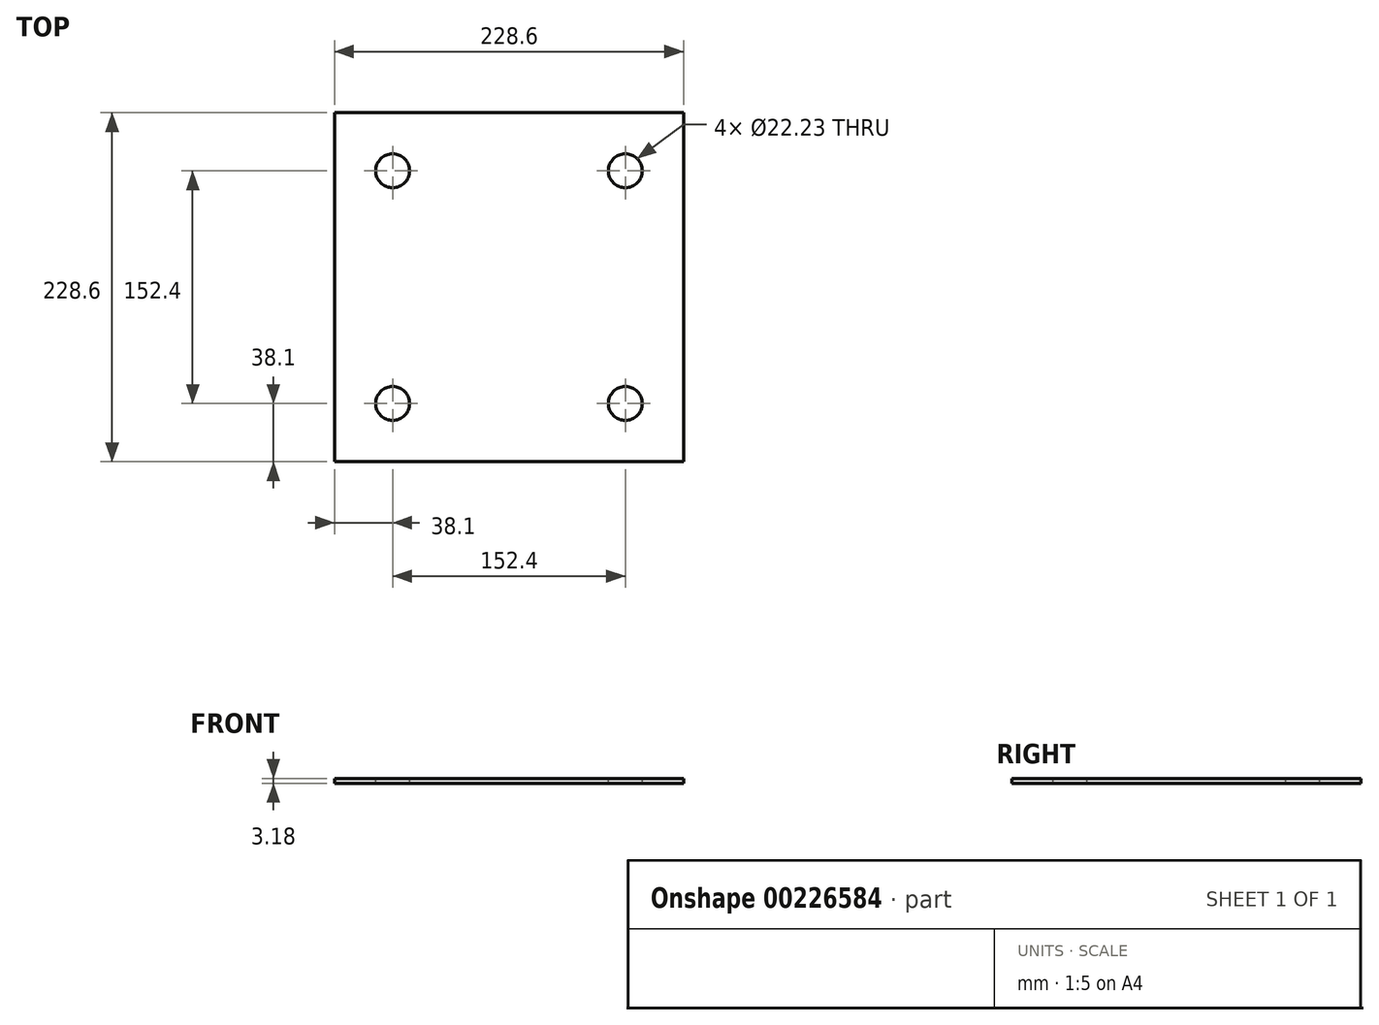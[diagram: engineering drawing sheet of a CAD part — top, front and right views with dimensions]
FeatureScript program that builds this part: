
annotation { "Feature Type Name" : "Feature", "Feature Type Description" : "" }
export const myFeature = defineFeature(function(context is Context, id is Id, definition is map)
    precondition{}
    {
        {
            var Q0;
            Q0=qCreatedBy(makeId("Top.planeOp"),FACE);
            var sketch = newSketch(context, id + "F0", { "sketchPlane" : qUnion([Q0])});
            skLineSegment(sketch, "E0.bottom", {"start": v(114.3, 114.3) * mm, "end": v(-114.3, 114.3) * mm});
            skLineSegment(sketch, "E0.top", {"start": v(114.3, -114.3) * mm, "end": v(-114.3, -114.3) * mm});
            skLineSegment(sketch, "E0.left", {"start": v(114.3, 114.3) * mm, "end": v(114.3, -114.3) * mm});
            skLineSegment(sketch, "E0.right", {"start": v(-114.3, 114.3) * mm, "end": v(-114.3, -114.3) * mm});
            skPoint(sketch, "E0.middle", {"position": v(0, 0) * mm});
            skSolve(sketch);
        }
        {
            var Q0;
            Q0=qSketchRegion(id+"F0",true);
            extrude(context, id + "F1", {"entities" : qUnion([Q0]), "oppositeDirection" : true, "depth" : 3.17 * mm, "symmetric" : true});
        }
        {
            var Q0;
            Q0=makeQuery(id+"F1.opExtrude","CAP_FACE",FACE,{"disambiguationData":[OSD([sQuery(id+"F0.wireOp",EDGE,"E0.bottom"),sQuery(id+"F0.wireOp",EDGE,"E0.top"),sQuery(id+"F0.wireOp",EDGE,"E0.left"),sQuery(id+"F0.wireOp",EDGE,"E0.right")])],"isStart":true});
            var sketch = newSketch(context, id + "F2", { "sketchPlane" : qUnion([Q0])});
            skLineSegment(sketch, "E1.bottom", {"start": v(76.2, 76.2) * mm, "end": v(-76.2, 76.2) * mm});
            skLineSegment(sketch, "E1.top", {"start": v(76.2, -76.2) * mm, "end": v(-76.2, -76.2) * mm});
            skLineSegment(sketch, "E1.left", {"start": v(76.2, 76.2) * mm, "end": v(76.2, -76.2) * mm});
            skLineSegment(sketch, "E1.right", {"start": v(-76.2, 76.2) * mm, "end": v(-76.2, -76.2) * mm});
            skPoint(sketch, "E1.middle", {"position": v(0, 0) * mm});
            skSolve(sketch);
        }
        {
            var Q0;
            Q0=sQuery(id+"F2.wireOp",VERTEX,"E1.right.start");
            var Q1;
            Q1=sQuery(id+"F2.wireOp",VERTEX,"E1.left.start");
            var Q2;
            Q2=sQuery(id+"F2.wireOp",VERTEX,"E1.top.end");
            var Q3;
            Q3=sQuery(id+"F2.wireOp",VERTEX,"E1.left.end");
            var Q4;
            Q4=makeQuery(id+"F1.opExtrude","SWEPT_BODY",BODY,{"disambiguationData":[OSD([sQuery(id+"F0.wireOp",EDGE,"E0.bottom"),sQuery(id+"F0.wireOp",EDGE,"E0.top"),sQuery(id+"F0.wireOp",EDGE,"E0.left"),sQuery(id+"F0.wireOp",EDGE,"E0.right")])]});
            hole(context, id + "F3", {"style" : HoleStyle.SIMPLE, "endStyle" : HoleEndStyle.THROUGH, "holeDiameter" : 22.22 * mm, "locations" : qUnion([Q0, Q1, Q2, Q3]), "scope" : qUnion([Q4]), "isTappedThrough" : true});
        }
    });
